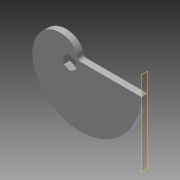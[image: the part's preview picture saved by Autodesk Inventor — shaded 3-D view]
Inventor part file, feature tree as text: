
AUTODESK INVENTOR PART (.ipt)
format: ipt  version: 2014 (Build 180170000, 170)  size: 113,664 bytes
history: native  units: in
note: dims shown in document units (in); Inventor stores cm internally (conversion verified against a paired STEP export)
features: plane x2, extrude x1, fillet x1, sketch x1, other x1
ambient origin geometry x8: Origin, YZ Plane, XZ Plane, XY Plane, X Axis, Y Axis, Z Axis, Center Point
bodies: Solid1 (feature_tree)
feature tree (6):
  extrude  "Extrusion1"  Depth=0.25in
  fillet  "Fillet1"  Radius=0.5in
  plane  "Work Plane2"
  sketch  "Sketch1"  dims[d0=1.7235in d1=2.3684in d7=0.25in d9=0.5in d10=0.6654in d11=8.4985in d12=2.17in d13=2.9281in d14=0.25in d15=0.0in d16=0.125in d17=-2.27in]
  other  "2D Equation Curve1"
  plane  "Work Plane1"
